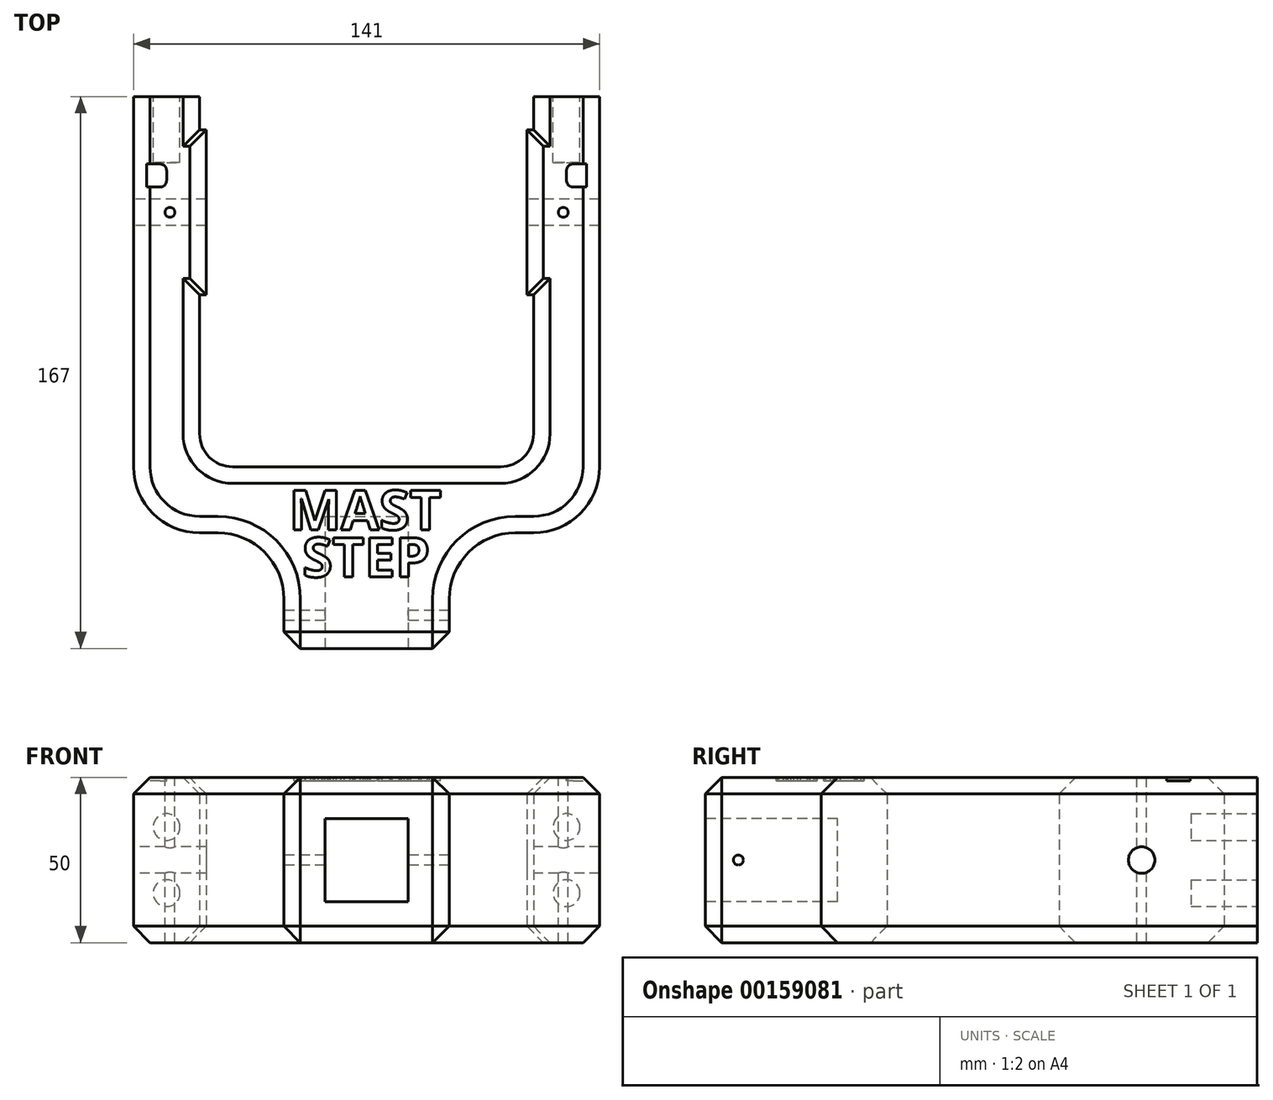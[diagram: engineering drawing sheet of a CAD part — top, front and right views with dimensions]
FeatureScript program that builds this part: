
annotation { "Feature Type Name" : "Feature", "Feature Type Description" : "" }
export const myFeature = defineFeature(function(context is Context, id is Id, definition is map)
    precondition{}
    {
        {
            var Q0;
            Q0=qCreatedBy(makeId("Top.planeOp"),FACE);
            var sketch = newSketch(context, id + "F0", { "sketchPlane" : qUnion([Q0])});
            skLineSegment(sketch, "E0", {"start": v(25, 0) * mm, "end": v(25, 15) * mm});
            skLineSegment(sketch, "E1", {"start": v(45, 35) * mm, "end": v(50.5, 35) * mm});
            skLineSegment(sketch, "E2", {"start": v(70.5, 55) * mm, "end": v(70.5, 157) * mm});
            skLineSegment(sketch, "E3", {"start": v(50.5, 157) * mm, "end": v(48.5, 157) * mm});
            skLineSegment(sketch, "E4", {"start": v(40.5, 55) * mm, "end": v(0, 55) * mm});
            skPoint(sketch, "E5.start.orphan", {"position": v(0, -9.98) * mm});
            skLineSegment(sketch, "E6", {"start": v(25, 0) * mm, "end": v(0, 0) * mm});
            skLineSegment(sketch, "E7", {"start": v(50.5, 65) * mm, "end": v(50.5, 107) * mm});
            skLineSegment(sketch, "E8", {"start": v(50.5, 107) * mm, "end": v(48.5, 107) * mm});
            skLineSegment(sketch, "E9", {"start": v(48.5, 107) * mm, "end": v(48.5, 157) * mm});
            skLineSegment(sketch, "E10.MirrorCS", {"start": v(-40.5, 55) * mm, "end": v(0, 55) * mm});
            skLineSegment(sketch, "E11.MirrorCS", {"start": v(-50.5, 65) * mm, "end": v(-50.5, 107) * mm});
            skLineSegment(sketch, "E12.MirrorCS", {"start": v(-50.5, 107) * mm, "end": v(-48.5, 107) * mm});
            skLineSegment(sketch, "E13.MirrorCS", {"start": v(-48.5, 107) * mm, "end": v(-48.5, 157) * mm});
            skLineSegment(sketch, "E14.MirrorCS", {"start": v(-50.5, 157) * mm, "end": v(-48.5, 157) * mm});
            skLineSegment(sketch, "E15.MirrorCS", {"start": v(-70.5, 55) * mm, "end": v(-70.5, 157) * mm});
            skLineSegment(sketch, "E16.MirrorCS", {"start": v(-45, 35) * mm, "end": v(-50.5, 35) * mm});
            skLineSegment(sketch, "E17.MirrorCS", {"start": v(-25, 0) * mm, "end": v(-25, 15) * mm});
            skLineSegment(sketch, "E18.MirrorCS", {"start": v(-25, 0) * mm, "end": v(0, 0) * mm});
            skPoint(sketch, "E19.visualSharp", {"position": v(-50.5, 55) * mm});
            skArc(sketch, "E19.filletArc", {"start": v(-50.5, 65) * mm, "mid": v(-47.57, 57.93) * mm, "end": v(-40.5, 55) * mm});
            skPoint(sketch, "E20.visualSharp", {"position": v(50.5, 55) * mm});
            skArc(sketch, "E20.filletArc", {"start": v(40.5, 55) * mm, "mid": v(47.57, 57.93) * mm, "end": v(50.5, 65) * mm});
            skPoint(sketch, "E21.visualSharp", {"position": v(-70.5, 35) * mm});
            skArc(sketch, "E21.filletArc", {"start": v(-70.5, 55) * mm, "mid": v(-64.64, 40.86) * mm, "end": v(-50.5, 35) * mm});
            skPoint(sketch, "E22.visualSharp", {"position": v(70.5, 35) * mm});
            skArc(sketch, "E22.filletArc", {"start": v(50.5, 35) * mm, "mid": v(64.64, 40.86) * mm, "end": v(70.5, 55) * mm});
            skPoint(sketch, "E23.visualSharp", {"position": v(25, 35) * mm});
            skArc(sketch, "E23.filletArc", {"start": v(45, 35) * mm, "mid": v(30.86, 29.14) * mm, "end": v(25, 15) * mm});
            skPoint(sketch, "E24.visualSharp", {"position": v(-25, 35) * mm});
            skArc(sketch, "E24.filletArc", {"start": v(-25, 15) * mm, "mid": v(-30.86, 29.14) * mm, "end": v(-45, 35) * mm});
            skLineSegment(sketch, "E25", {"start": v(70.5, 167) * mm, "end": v(70.5, 157) * mm});
            skLineSegment(sketch, "E26", {"start": v(-95.94, 132) * mm, "end": v(111.6, 132) * mm, "construction": true});
            skPoint(sketch, "E26.startSnap0", {"position": v(-48.5, 132) * mm});
            skLineSegment(sketch, "E27", {"start": v(50.5, 167) * mm, "end": v(50.5, 157) * mm});
            skLineSegment(sketch, "E28.MirrorCS", {"start": v(-70.5, 167) * mm, "end": v(-70.5, 157) * mm});
            skLineSegment(sketch, "E29.MirrorCS", {"start": v(-50.5, 167) * mm, "end": v(-50.5, 157) * mm});
            skPoint(sketch, "E30.orphan", {"position": v(-70.5, 157) * mm});
            skLineSegment(sketch, "E31", {"start": v(-70.5, 167) * mm, "end": v(-50.5, 167) * mm});
            skLineSegment(sketch, "E32.trimOffspring", {"start": v(50.5, 167) * mm, "end": v(70.5, 167) * mm});
            skSolve(sketch);
        }
        {
            var Q0;
            Q0=qSketchRegion(id+"F0",true);
            extrude(context, id + "F1", {"entities" : qUnion([Q0]), "depth" : 25 * mm, "hasSecondDirection" : true, "secondDirectionOppositeDirection" : true, "secondDirectionDepth" : 25 * mm});
        }
        {
            var Q0;
            Q0=makeQuery(id+"F1.opExtrude","SWEPT_FACE",FACE,{"disambiguationData":[OSD([sQuery(id+"F0.wireOp",EDGE,"E6"),sQuery(id+"F0.wireOp",EDGE,"E18.MirrorCS")])]});
            var sketch = newSketch(context, id + "F2", { "sketchPlane" : qUnion([Q0])});
            skLineSegment(sketch, "E33.bottom", {"start": v(-12.6, -12.6) * mm, "end": v(12.6, -12.6) * mm});
            skLineSegment(sketch, "E33.top", {"start": v(-12.6, 12.6) * mm, "end": v(12.6, 12.6) * mm});
            skLineSegment(sketch, "E33.left", {"start": v(-12.6, -12.6) * mm, "end": v(-12.6, 12.6) * mm});
            skLineSegment(sketch, "E33.right", {"start": v(12.6, -12.6) * mm, "end": v(12.6, 12.6) * mm});
            skSolve(sketch);
        }
        {
            var Q0;
            Q0=qSketchRegion(id+"F2",true);
            extrude(context, id + "F3", {"entities" : qUnion([Q0]), "operationType" : NewBodyOperationType.REMOVE, "oppositeDirection" : true, "depth" : 40 * mm});
        }
        {
            var Q0;
            Q0=makeQuery(id+"F1.opExtrude","SWEPT_FACE",FACE,{"disambiguationData":[OSD([sQuery(id+"F0.wireOp",EDGE,"E15.MirrorCS")])]});
            var sketch = newSketch(context, id + "F4", { "sketchPlane" : qUnion([Q0])});
            skLineSegment(sketch, "E34.0", {"start": v(-55, 20) * mm, "end": v(-55, -20) * mm, "construction": true});
            skCircle(sketch, "E35", {"center": v(-132, 0) * mm, "radius": 4 * mm});
            skSolve(sketch);
        }
        {
            var Q0;
            Q0=qSketchRegion(id+"F4",true);
            extrude(context, id + "F5", {"entities" : qUnion([Q0]), "operationType" : NewBodyOperationType.REMOVE, "endBound" : BoundingType.THROUGH_ALL, "oppositeDirection" : true, "depth" : 25 * mm});
        }
        {
            var Q0;
            Q0=makeQuery(id+"F1.opExtrude","SWEPT_EDGE",EDGE,{"disambiguationData":[OSD([sQuery(id+"F0.wireOp",EDGE,"E0"),sQuery(id+"F0.wireOp",EDGE,"E6")])]});
            var Q1;
            Q1=makeQuery(id+"F1.opExtrude","SWEPT_EDGE",EDGE,{"disambiguationData":[OSD([sQuery(id+"F0.wireOp",EDGE,"E17.MirrorCS"),sQuery(id+"F0.wireOp",EDGE,"E18.MirrorCS")])]});
            var Q2;
            Q2=makeQuery(id+"F1.opExtrude","CAP_EDGE",EDGE,{"disambiguationData":[OSD([sQuery(id+"F0.wireOp",EDGE,"E24.filletArc")])],"isStart":false});
            var Q3;
            Q3=makeQuery(id+"F1.opExtrude","CAP_EDGE",EDGE,{"disambiguationData":[OSD([sQuery(id+"F0.wireOp",EDGE,"E17.MirrorCS")])],"isStart":false});
            var Q4;
            Q4=makeQuery(id+"F1.opExtrude","CAP_EDGE",EDGE,{"disambiguationData":[OSD([sQuery(id+"F0.wireOp",EDGE,"E16.MirrorCS")])],"isStart":false});
            var Q5;
            Q5=makeQuery(id+"F1.opExtrude","CAP_EDGE",EDGE,{"disambiguationData":[OSD([sQuery(id+"F0.wireOp",EDGE,"E21.filletArc")])],"isStart":false});
            var Q6;
            Q6=makeQuery(id+"F1.opExtrude","CAP_EDGE",EDGE,{"disambiguationData":[OSD([sQuery(id+"F0.wireOp",EDGE,"E15.MirrorCS"),sQuery(id+"F0.wireOp",EDGE,"E28.MirrorCS")])],"isStart":false});
            var Q7;
            Q7=makeQuery(id+"F1.opExtrude","CAP_EDGE",EDGE,{"disambiguationData":[OSD([sQuery(id+"F0.wireOp",EDGE,"E11.MirrorCS")])],"isStart":false});
            var Q8;
            Q8=makeQuery(id+"F1.opExtrude","CAP_EDGE",EDGE,{"disambiguationData":[OSD([sQuery(id+"F0.wireOp",EDGE,"E13.MirrorCS")])],"isStart":false});
            var Q9;
            Q9=makeQuery(id+"F1.opExtrude","CAP_EDGE",EDGE,{"disambiguationData":[OSD([sQuery(id+"F0.wireOp",EDGE,"E29.MirrorCS")])],"isStart":false});
            var Q10;
            Q10=makeQuery(id+"F1.opExtrude","CAP_EDGE",EDGE,{"disambiguationData":[OSD([sQuery(id+"F0.wireOp",EDGE,"E19.filletArc")])],"isStart":false});
            var Q11;
            Q11=makeQuery(id+"F1.opExtrude","CAP_EDGE",EDGE,{"disambiguationData":[OSD([sQuery(id+"F0.wireOp",EDGE,"E4"),sQuery(id+"F0.wireOp",EDGE,"E10.MirrorCS")])],"isStart":false});
            var Q12;
            Q12=makeQuery(id+"F1.opExtrude","CAP_EDGE",EDGE,{"disambiguationData":[OSD([sQuery(id+"F0.wireOp",EDGE,"E20.filletArc")])],"isStart":false});
            var Q13;
            Q13=makeQuery(id+"F1.opExtrude","CAP_EDGE",EDGE,{"disambiguationData":[OSD([sQuery(id+"F0.wireOp",EDGE,"E7")])],"isStart":false});
            var Q14;
            Q14=makeQuery(id+"F1.opExtrude","CAP_EDGE",EDGE,{"disambiguationData":[OSD([sQuery(id+"F0.wireOp",EDGE,"E9")])],"isStart":false});
            var Q15;
            Q15=makeQuery(id+"F1.opExtrude","CAP_EDGE",EDGE,{"disambiguationData":[OSD([sQuery(id+"F0.wireOp",EDGE,"E27")])],"isStart":false});
            var Q16;
            Q16=makeQuery(id+"F1.opExtrude","CAP_EDGE",EDGE,{"disambiguationData":[OSD([sQuery(id+"F0.wireOp",EDGE,"E2"),sQuery(id+"F0.wireOp",EDGE,"E25")])],"isStart":false});
            var Q17;
            Q17=makeQuery(id+"F1.opExtrude","CAP_EDGE",EDGE,{"disambiguationData":[OSD([sQuery(id+"F0.wireOp",EDGE,"E22.filletArc")])],"isStart":false});
            var Q18;
            Q18=makeQuery(id+"F1.opExtrude","CAP_EDGE",EDGE,{"disambiguationData":[OSD([sQuery(id+"F0.wireOp",EDGE,"E23.filletArc")])],"isStart":false});
            var Q19;
            Q19=makeQuery(id+"F1.opExtrude","CAP_EDGE",EDGE,{"disambiguationData":[OSD([sQuery(id+"F0.wireOp",EDGE,"E1")])],"isStart":false});
            var Q20;
            Q20=makeQuery(id+"F1.opExtrude","CAP_EDGE",EDGE,{"disambiguationData":[OSD([sQuery(id+"F0.wireOp",EDGE,"E0")])],"isStart":false});
            var Q21;
            Q21=makeQuery(id+"F1.opExtrude","CAP_EDGE",EDGE,{"disambiguationData":[OSD([sQuery(id+"F0.wireOp",EDGE,"E6"),sQuery(id+"F0.wireOp",EDGE,"E18.MirrorCS")])],"isStart":false});
            var Q22;
            Q22=makeQuery(id+"F1.opExtrude","CAP_EDGE",EDGE,{"disambiguationData":[OSD([sQuery(id+"F0.wireOp",EDGE,"E8")])],"isStart":false});
            var Q23;
            Q23=makeQuery(id+"F1.opExtrude","CAP_EDGE",EDGE,{"disambiguationData":[OSD([sQuery(id+"F0.wireOp",EDGE,"E3")])],"isStart":false});
            var Q24;
            Q24=makeQuery(id+"F1.opExtrude","CAP_EDGE",EDGE,{"disambiguationData":[OSD([sQuery(id+"F0.wireOp",EDGE,"E14.MirrorCS")])],"isStart":false});
            var Q25;
            Q25=makeQuery(id+"F1.opExtrude","CAP_EDGE",EDGE,{"disambiguationData":[OSD([sQuery(id+"F0.wireOp",EDGE,"E12.MirrorCS")])],"isStart":false});
            var Q26;
            Q26=makeQuery(id+"F1.opExtrude","CAP_EDGE",EDGE,{"disambiguationData":[OSD([sQuery(id+"F0.wireOp",EDGE,"E2"),sQuery(id+"F0.wireOp",EDGE,"E25")])],"isStart":true});
            var Q27;
            Q27=makeQuery(id+"F1.opExtrude","CAP_EDGE",EDGE,{"disambiguationData":[OSD([sQuery(id+"F0.wireOp",EDGE,"E7")])],"isStart":true});
            var Q28;
            Q28=makeQuery(id+"F1.opExtrude","CAP_EDGE",EDGE,{"disambiguationData":[OSD([sQuery(id+"F0.wireOp",EDGE,"E9")])],"isStart":true});
            var Q29;
            Q29=makeQuery(id+"F1.opExtrude","CAP_EDGE",EDGE,{"disambiguationData":[OSD([sQuery(id+"F0.wireOp",EDGE,"E27")])],"isStart":true});
            var Q30;
            Q30=makeQuery(id+"F1.opExtrude","CAP_EDGE",EDGE,{"disambiguationData":[OSD([sQuery(id+"F0.wireOp",EDGE,"E3")])],"isStart":true});
            var Q31;
            Q31=makeQuery(id+"F1.opExtrude","CAP_EDGE",EDGE,{"disambiguationData":[OSD([sQuery(id+"F0.wireOp",EDGE,"E8")])],"isStart":true});
            var Q32;
            Q32=makeQuery(id+"F1.opExtrude","CAP_EDGE",EDGE,{"disambiguationData":[OSD([sQuery(id+"F0.wireOp",EDGE,"E20.filletArc")])],"isStart":true});
            var Q33;
            Q33=makeQuery(id+"F1.opExtrude","CAP_EDGE",EDGE,{"disambiguationData":[OSD([sQuery(id+"F0.wireOp",EDGE,"E4"),sQuery(id+"F0.wireOp",EDGE,"E10.MirrorCS")])],"isStart":true});
            var Q34;
            Q34=makeQuery(id+"F1.opExtrude","CAP_EDGE",EDGE,{"disambiguationData":[OSD([sQuery(id+"F0.wireOp",EDGE,"E19.filletArc")])],"isStart":true});
            var Q35;
            Q35=makeQuery(id+"F1.opExtrude","CAP_EDGE",EDGE,{"disambiguationData":[OSD([sQuery(id+"F0.wireOp",EDGE,"E11.MirrorCS")])],"isStart":true});
            var Q36;
            Q36=makeQuery(id+"F1.opExtrude","CAP_EDGE",EDGE,{"disambiguationData":[OSD([sQuery(id+"F0.wireOp",EDGE,"E12.MirrorCS")])],"isStart":true});
            var Q37;
            Q37=makeQuery(id+"F1.opExtrude","CAP_EDGE",EDGE,{"disambiguationData":[OSD([sQuery(id+"F0.wireOp",EDGE,"E13.MirrorCS")])],"isStart":true});
            var Q38;
            Q38=makeQuery(id+"F1.opExtrude","CAP_EDGE",EDGE,{"disambiguationData":[OSD([sQuery(id+"F0.wireOp",EDGE,"E14.MirrorCS")])],"isStart":true});
            var Q39;
            Q39=makeQuery(id+"F1.opExtrude","CAP_EDGE",EDGE,{"disambiguationData":[OSD([sQuery(id+"F0.wireOp",EDGE,"E29.MirrorCS")])],"isStart":true});
            var Q40;
            Q40=makeQuery(id+"F1.opExtrude","CAP_EDGE",EDGE,{"disambiguationData":[OSD([sQuery(id+"F0.wireOp",EDGE,"E22.filletArc")])],"isStart":true});
            var Q41;
            Q41=makeQuery(id+"F1.opExtrude","CAP_EDGE",EDGE,{"disambiguationData":[OSD([sQuery(id+"F0.wireOp",EDGE,"E1")])],"isStart":true});
            var Q42;
            Q42=makeQuery(id+"F1.opExtrude","CAP_EDGE",EDGE,{"disambiguationData":[OSD([sQuery(id+"F0.wireOp",EDGE,"E23.filletArc")])],"isStart":true});
            var Q43;
            Q43=makeQuery(id+"F1.opExtrude","CAP_EDGE",EDGE,{"disambiguationData":[OSD([sQuery(id+"F0.wireOp",EDGE,"E0")])],"isStart":true});
            var Q44;
            Q44=makeQuery(id+"F1.opExtrude","CAP_EDGE",EDGE,{"disambiguationData":[OSD([sQuery(id+"F0.wireOp",EDGE,"E6"),sQuery(id+"F0.wireOp",EDGE,"E18.MirrorCS")])],"isStart":true});
            var Q45;
            Q45=makeQuery(id+"F1.opExtrude","CAP_EDGE",EDGE,{"disambiguationData":[OSD([sQuery(id+"F0.wireOp",EDGE,"E17.MirrorCS")])],"isStart":true});
            var Q46;
            Q46=makeQuery(id+"F1.opExtrude","CAP_EDGE",EDGE,{"disambiguationData":[OSD([sQuery(id+"F0.wireOp",EDGE,"E24.filletArc")])],"isStart":true});
            var Q47;
            Q47=makeQuery(id+"F1.opExtrude","CAP_EDGE",EDGE,{"disambiguationData":[OSD([sQuery(id+"F0.wireOp",EDGE,"E16.MirrorCS")])],"isStart":true});
            var Q48;
            Q48=makeQuery(id+"F1.opExtrude","CAP_EDGE",EDGE,{"disambiguationData":[OSD([sQuery(id+"F0.wireOp",EDGE,"E21.filletArc")])],"isStart":true});
            var Q49;
            Q49=makeQuery(id+"F1.opExtrude","CAP_EDGE",EDGE,{"disambiguationData":[OSD([sQuery(id+"F0.wireOp",EDGE,"E15.MirrorCS"),sQuery(id+"F0.wireOp",EDGE,"E28.MirrorCS")])],"isStart":true});
            chamfer(context, id + "F6", {"entities" : qUnion([Q0, Q1, Q2, Q3, Q4, Q5, Q6, Q7, Q8, Q9, Q10, Q11, Q12, Q13, Q14, Q15, Q16, Q17, Q18, Q19, Q20, Q21, Q22, Q23, Q24, Q25, Q26, Q27, Q28, Q29, Q30, Q31, Q32, Q33, Q34, Q35, Q36, Q37, Q38, Q39, Q40, Q41, Q42, Q43, Q44, Q45, Q46, Q47, Q48, Q49]), "width" : 5 * mm, "tangentPropagation" : true});
        }
        {
            var Q0;
            Q0=makeQuery(id+"F1.opExtrude","CAP_FACE",FACE,{"disambiguationData":[OSD([sQuery(id+"F0.wireOp",EDGE,"E0"),sQuery(id+"F0.wireOp",EDGE,"E1"),sQuery(id+"F0.wireOp",EDGE,"E2"),sQuery(id+"F0.wireOp",EDGE,"E3"),sQuery(id+"F0.wireOp",EDGE,"E4"),sQuery(id+"F0.wireOp",EDGE,"E6"),sQuery(id+"F0.wireOp",EDGE,"E7"),sQuery(id+"F0.wireOp",EDGE,"E8"),sQuery(id+"F0.wireOp",EDGE,"E9"),sQuery(id+"F0.wireOp",EDGE,"E10.MirrorCS"),sQuery(id+"F0.wireOp",EDGE,"E11.MirrorCS"),sQuery(id+"F0.wireOp",EDGE,"E12.MirrorCS"),sQuery(id+"F0.wireOp",EDGE,"E13.MirrorCS"),sQuery(id+"F0.wireOp",EDGE,"E14.MirrorCS"),sQuery(id+"F0.wireOp",EDGE,"E15.MirrorCS"),sQuery(id+"F0.wireOp",EDGE,"E16.MirrorCS"),sQuery(id+"F0.wireOp",EDGE,"E17.MirrorCS"),sQuery(id+"F0.wireOp",EDGE,"E18.MirrorCS"),sQuery(id+"F0.wireOp",EDGE,"E19.filletArc"),sQuery(id+"F0.wireOp",EDGE,"E20.filletArc"),sQuery(id+"F0.wireOp",EDGE,"E21.filletArc"),sQuery(id+"F0.wireOp",EDGE,"E22.filletArc"),sQuery(id+"F0.wireOp",EDGE,"E23.filletArc"),sQuery(id+"F0.wireOp",EDGE,"E24.filletArc"),sQuery(id+"F0.wireOp",EDGE,"w6YjvgSy-DeMm-ak1Y-v2mC-BKVpjcGkXHr8"),sQuery(id+"F0.wireOp",EDGE,"K7Ft8JkS-qjwj-awK3-6d26-UwzgPMIYWqw9"),sQuery(id+"F0.wireOp",EDGE,"E25"),sQuery(id+"F0.wireOp",EDGE,"E27"),sQuery(id+"F0.wireOp",EDGE,"6bc5deb2-0fe5-4606-a96e-79efeb6a55a9.filletArc"),sQuery(id+"F0.wireOp",EDGE,"d4b485c1-665c-44cb-8105-eee5d3987f97.filletArc"),sQuery(id+"F0.wireOp",EDGE,"50617510-5b01-4a37-ae00-ff8a952e2e2f"),sQuery(id+"F0.wireOp",EDGE,"E28.MirrorCS"),sQuery(id+"F0.wireOp",EDGE,"E29.MirrorCS"),sQuery(id+"F0.wireOp",EDGE,"4657d517-9da0-495f-adf9-4d8d8cb34cdf0.MirrorCS"),sQuery(id+"F0.wireOp",EDGE,"de587e12-b232-430f-ad0f-d92d56e971cb0.MirrorCS"),sQuery(id+"F0.wireOp",EDGE,"b9e9465a-1cd0-43f2-8ff1-77882957a7b30.MirrorCS"),sQuery(id+"F0.wireOp",EDGE,"6bddaa20-09ad-44ad-8433-ee7bcf0af6580.MirrorCS"),sQuery(id+"F0.wireOp",EDGE,"ea40cd34-fc4b-4a22-b093-bc6e3d75892b0.MirrorCS")])],"isStart":false});
            var sketch = newSketch(context, id + "F7", { "sketchPlane" : qUnion([Q0])});
            skLineSegment(sketch, "E36", {"start": v(-70.5, 132) * mm, "end": v(-48.5, 132) * mm, "construction": true});
            skPoint(sketch, "E36.endSnap0", {"position": v(48.5, 132) * mm});
            skCircle(sketch, "E37", {"center": v(-59.5, 132) * mm, "radius": 1.5 * mm});
            skCircle(sketch, "E38", {"center": v(59.5, 132) * mm, "radius": 1.5 * mm});
            skPoint(sketch, "E39", {"position": v(-48.5, 132) * mm});
            skPoint(sketch, "E40", {"position": v(-70.5, 132) * mm});
            skLineSegment(sketch, "E41.trimOffspring", {"start": v(48.5, 132) * mm, "end": v(70.5, 132) * mm, "construction": true});
            skPoint(sketch, "E42", {"position": v(70.5, 132) * mm});
            skPoint(sketch, "E43.orphan", {"position": v(109.82, 132) * mm});
            skSolve(sketch);
        }
        {
            var Q0;
            Q0 = qSketchRegion(id + "F7", true);
            extrude(context, id + "F8", {"entities" : qUnion([Q0]), "operationType" : NewBodyOperationType.REMOVE, "endBound" : BoundingType.THROUGH_ALL, "oppositeDirection" : true, "depth" : 25 * mm});
        }
        {
            var Q0;
            Q0=makeQuery(id+"F1.opExtrude","SWEPT_FACE",FACE,{"disambiguationData":[OSD([sQuery(id+"F0.wireOp",EDGE,"E17.MirrorCS")])]});
            var sketch = newSketch(context, id + "F9", { "sketchPlane" : qUnion([Q0])});
            skLineSegment(sketch, "E44", {"start": v(-15, 0) * mm, "end": v(-5, 0) * mm, "construction": true});
            skCircle(sketch, "E45", {"center": v(-10, 0) * mm, "radius": 1.5 * mm});
            skSolve(sketch);
        }
        {
            var Q0;
            Q0 = qSketchRegion(id + "F9", true);
            extrude(context, id + "F10", {"entities" : qUnion([Q0]), "operationType" : NewBodyOperationType.REMOVE, "endBound" : BoundingType.THROUGH_ALL, "oppositeDirection" : true, "depth" : 25 * mm});
        }
        {
            var Q0;
            Q0=makeQuery(id+"F1.opExtrude","CAP_FACE",FACE,{"disambiguationData":[OSD([sQuery(id+"F0.wireOp",EDGE,"E0"),sQuery(id+"F0.wireOp",EDGE,"E1"),sQuery(id+"F0.wireOp",EDGE,"E2"),sQuery(id+"F0.wireOp",EDGE,"E3"),sQuery(id+"F0.wireOp",EDGE,"E4"),sQuery(id+"F0.wireOp",EDGE,"E6"),sQuery(id+"F0.wireOp",EDGE,"E7"),sQuery(id+"F0.wireOp",EDGE,"E8"),sQuery(id+"F0.wireOp",EDGE,"E9"),sQuery(id+"F0.wireOp",EDGE,"E10.MirrorCS"),sQuery(id+"F0.wireOp",EDGE,"E11.MirrorCS"),sQuery(id+"F0.wireOp",EDGE,"E12.MirrorCS"),sQuery(id+"F0.wireOp",EDGE,"E13.MirrorCS"),sQuery(id+"F0.wireOp",EDGE,"E14.MirrorCS"),sQuery(id+"F0.wireOp",EDGE,"E15.MirrorCS"),sQuery(id+"F0.wireOp",EDGE,"E16.MirrorCS"),sQuery(id+"F0.wireOp",EDGE,"E17.MirrorCS"),sQuery(id+"F0.wireOp",EDGE,"E18.MirrorCS"),sQuery(id+"F0.wireOp",EDGE,"E19.filletArc"),sQuery(id+"F0.wireOp",EDGE,"E20.filletArc"),sQuery(id+"F0.wireOp",EDGE,"E21.filletArc"),sQuery(id+"F0.wireOp",EDGE,"E22.filletArc"),sQuery(id+"F0.wireOp",EDGE,"E23.filletArc"),sQuery(id+"F0.wireOp",EDGE,"E24.filletArc"),sQuery(id+"F0.wireOp",EDGE,"w6YjvgSy-DeMm-ak1Y-v2mC-BKVpjcGkXHr8"),sQuery(id+"F0.wireOp",EDGE,"K7Ft8JkS-qjwj-awK3-6d26-UwzgPMIYWqw9"),sQuery(id+"F0.wireOp",EDGE,"E25"),sQuery(id+"F0.wireOp",EDGE,"E27"),sQuery(id+"F0.wireOp",EDGE,"6bc5deb2-0fe5-4606-a96e-79efeb6a55a9.filletArc"),sQuery(id+"F0.wireOp",EDGE,"d4b485c1-665c-44cb-8105-eee5d3987f97.filletArc"),sQuery(id+"F0.wireOp",EDGE,"50617510-5b01-4a37-ae00-ff8a952e2e2f"),sQuery(id+"F0.wireOp",EDGE,"E28.MirrorCS"),sQuery(id+"F0.wireOp",EDGE,"E29.MirrorCS"),sQuery(id+"F0.wireOp",EDGE,"4657d517-9da0-495f-adf9-4d8d8cb34cdf0.MirrorCS"),sQuery(id+"F0.wireOp",EDGE,"de587e12-b232-430f-ad0f-d92d56e971cb0.MirrorCS"),sQuery(id+"F0.wireOp",EDGE,"b9e9465a-1cd0-43f2-8ff1-77882957a7b30.MirrorCS"),sQuery(id+"F0.wireOp",EDGE,"6bddaa20-09ad-44ad-8433-ee7bcf0af6580.MirrorCS"),sQuery(id+"F0.wireOp",EDGE,"ea40cd34-fc4b-4a22-b093-bc6e3d75892b0.MirrorCS")])],"isStart":false});
            var sketch = newSketch(context, id + "F11", { "sketchPlane" : qUnion([Q0])});
            skText(sketch, "E46", { "text": "MAST", "fontName": "OpenSans-Bold.ttf"});
            skPoint(sketch, "E47", {"position": v(0, 50) * mm});
            skText(sketch, "E48", { "text": "STEP", "fontName": "OpenSans-Bold.ttf"});
            skLineSegment(sketch, "E49.bottom", {"start": v(62.5, 146.62) * mm, "end": v(70.5, 146.62) * mm});
            skLineSegment(sketch, "E49.top", {"start": v(62.5, 139.62) * mm, "end": v(70.5, 139.62) * mm});
            skLineSegment(sketch, "E49.left", {"start": v(60.5, 144.62) * mm, "end": v(60.5, 141.62) * mm});
            skLineSegment(sketch, "E49.right", {"start": v(70.5, 146.62) * mm, "end": v(70.5, 139.62) * mm});
            skPoint(sketch, "E49.middle", {"position": v(65.5, 143.12) * mm});
            skPoint(sketch, "E50.visualSharp", {"position": v(60.5, 146.62) * mm});
            skArc(sketch, "E50.filletArc", {"start": v(62.5, 146.62) * mm, "mid": v(61.09, 146.04) * mm, "end": v(60.5, 144.62) * mm});
            skPoint(sketch, "E51.visualSharp", {"position": v(60.5, 139.62) * mm});
            skArc(sketch, "E51.filletArc", {"start": v(60.5, 141.62) * mm, "mid": v(61.09, 140.2) * mm, "end": v(62.5, 139.62) * mm});
            skLineSegment(sketch, "E52.MirrorCS", {"start": v(-60.5, 144.62) * mm, "end": v(-60.5, 141.62) * mm});
            skArc(sketch, "E53.MirrorCS", {"start": v(-62.5, 146.62) * mm, "mid": v(-61.09, 146.04) * mm, "end": v(-60.5, 144.62) * mm});
            skArc(sketch, "E54.MirrorCS", {"start": v(-60.5, 141.62) * mm, "mid": v(-61.09, 140.2) * mm, "end": v(-62.5, 139.62) * mm});
            skPoint(sketch, "E55.MirrorP", {"position": v(-60.5, 139.62) * mm});
            skLineSegment(sketch, "E56.MirrorCS", {"start": v(-62.5, 139.62) * mm, "end": v(-70.5, 139.62) * mm});
            skLineSegment(sketch, "E57.MirrorCS", {"start": v(-70.5, 146.62) * mm, "end": v(-70.5, 139.62) * mm});
            skLineSegment(sketch, "E58.MirrorCS", {"start": v(-62.5, 146.62) * mm, "end": v(-70.5, 146.62) * mm});
            skPoint(sketch, "E59.MirrorP", {"position": v(-65.5, 143.12) * mm});
            skPoint(sketch, "E60.MirrorP", {"position": v(-60.5, 146.62) * mm});
            const initialGuessF11  = {"E46": [-0.0234, 0.03593, 1, 0, 0.012], "E48": [-0.01948, 0.02165, 1, 0, 0.012]};
            skSetInitialGuess(sketch, initialGuessF11);
            skSolve(sketch);
        }
        {
            var Q0;
            Q0 = qSketchRegion(id + "F11", true);
            extrude(context, id + "F12", {"entities" : qUnion([Q0]), "operationType" : NewBodyOperationType.REMOVE, "oppositeDirection" : true, "depth" : 1 * mm});
        }
        {
            var Q0;
            Q0=makeQuery(id+"F1.opExtrude","SWEPT_FACE",FACE,{"disambiguationData":[OSD([sQuery(id+"F0.wireOp",EDGE,"E32.trimOffspring")])]});
            var sketch = newSketch(context, id + "F13", { "sketchPlane" : qUnion([Q0])});
            skLineSegment(sketch, "E61", {"start": v(-70.5, 0) * mm, "end": v(-50.5, 0) * mm, "construction": true});
            skLineSegment(sketch, "E62", {"start": v(70.5, 0) * mm, "end": v(50.5, 0) * mm, "construction": true});
            skCircle(sketch, "E63", {"center": v(60.5, -10) * mm, "radius": 4.05 * mm});
            skCircle(sketch, "E64", {"center": v(60.5, 10) * mm, "radius": 4.05 * mm});
            skCircle(sketch, "E65", {"center": v(-60.5, -10) * mm, "radius": 4.05 * mm});
            skCircle(sketch, "E66", {"center": v(-60.5, 10) * mm, "radius": 4.05 * mm});
            skPoint(sketch, "E67", {"position": v(60.5, 0) * mm});
            skPoint(sketch, "E68", {"position": v(-60.5, 0) * mm});
            skSolve(sketch);
        }
        {
            var Q0;
            Q0 = qSketchRegion(id + "F13", true);
            extrude(context, id + "F14", {"entities" : qUnion([Q0]), "operationType" : NewBodyOperationType.REMOVE, "oppositeDirection" : true, "depth" : 20 * mm});
        }
    });
